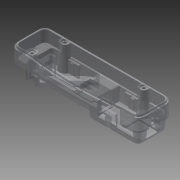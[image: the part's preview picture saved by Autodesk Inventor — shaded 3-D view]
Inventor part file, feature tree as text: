
AUTODESK INVENTOR PART (.ipt)
format: ipt  version: 2014 SP1 (Build 180222100, 222)  size: 1,254,400 bytes
history: native  units: mm
features: sketch x33, extrude x30, fillet x5, other x2, sweep x1, shell x1
ambient origin geometry x8: Origin, YZ Plane, XZ Plane, XY Plane, X Axis, Y Axis, Z Axis, Center Point
bodies: Solid1 (feature_tree)
feature tree (72):
  extrude  "MainShape"  Depth=38.0mm
  extrude  "LowerCurve"  Depth=70.0mm
  extrude  "RearShell"  Depth=8.0mm
  extrude  "LinkCableIndent"  Depth=3.5mm
  extrude  "LinkCableRecess"  Depth=30.0mm
  sweep  "LnkCableRecessSlanti"
  extrude  "ClipSlotsTop"  Depth=15.0mm
  extrude  "ClipSlotsBottom"  Depth=18.0mm
  extrude  "LinkCableSlot"  Depth=2.0mm
  shell  "HollowShell"  Thickness=2.0mm
  extrude  "USBCutout"  Depth=10.0mm
  extrude  "LinkCableCuttout"  Depth=13.5mm
  extrude  "LockingClipSlot"  Depth=16.0mm
  fillet  "RearRoundLarge"  Radius=9.0mm
  fillet  "RearRoundSmall"  Radius=3.0mm
  extrude  "PCBSideShelf"  TaperAngle=0.0deg  [1 undecoded]
  extrude  "PCBRearShelf"  TaperAngle=45.0deg  [1 undecoded]
  extrude  "PCBUSBShelf"  Depth=15.0mm
  extrude  "USBCutoutInternal"  TaperAngle=0.0deg  [1 undecoded]
  extrude  "FrontExtension"  TaperAngle=0.0deg  [1 undecoded]
  other  "FrontLip"
  extrude  "USBCuttoutReduction"  Depth=20.0mm
  extrude  "Extrusion19"  Depth=15.0mm
  fillet  "PCBInternalRadius"  Radius=33.0mm
  sketch  "Sketch22"  dims[d64=6.1mm d65=6.1mm]
  extrude  "RearLockingClip"  Depth=6.1mm
  extrude  "PCBSupport"  Depth=10.0mm
  extrude  "DCJackCuttout"  Depth=2.0mm
  extrude  "DCJackInternalSupport"  Depth=1.0mm
  extrude  "DCJackVoltageRef"  Depth=4.0mm TaperAngle=0.0deg
  extrude  "LabelIndent"  Depth=6.0mm
  other  "MountingBoss"
  extrude  "MountingBossLipCleanup"  Depth=2.0mm
  extrude  "MountingBossRearCleanup"  Depth=1.0mm
  fillet  "MountingBossRearRounds"  [1 undecoded]
  extrude  "LEDCutouts"  Depth=10.0mm
  extrude  "PCBEndstop"  Depth=10.0mm
  extrude  "PCBRearstop"  Depth=1.5mm
  extrude  "3DPrintingOptimisation"  Depth=15.0mm
  fillet  "3DPrinitingOptimisationRound"  Radius=12.0mm
  sketch  "Sketch2"  dims[d0=19.0mm d1=38.0mm]
  sketch  "Sketch4"  dims[d2=140.0mm d3=70.0mm]
  sketch  "Sketch5"  dims[d4=8.0mm d5=8.0mm]
  sketch  "Sketch6"  dims[d6=5.0mm d7=0.0mm d12=3.5mm]
  sketch  "Sketch7"  dims[d17=5.0mm d18=0.0mm d24=30.0mm]
  sketch  "Sketch8"  dims[d25=30.0mm d26=18.0mm]
  sketch  "Sketch9"  dims[d27=15.0mm d28=15.0mm]
  sketch  "Sketch10"  dims[d30=2.0mm d31=18.0mm]
  sketch  "Sketch11"  dims[d32=5.5mm d33=2.0mm d34=2.0mm]
  sketch  "Sketch12"  dims[d35=2.0mm d36=10.0mm]
  sketch  "Sketch13"  dims[d37=6.0mm d38=13.5mm d39=-0.872665mm]
  sketch  "Sketch14"  dims[d41=54.0mm d42=16.0mm d43=9.0mm d44=3.0mm]
  sketch  "Sketch15"  dims[d45=15.0mm d46=0.0mm d47=0.0mm]
  sketch  "Sketch16"  dims[d48=0.0mm d50=45.0deg]
  sketch  "Sketch17"  dims[d51=15.0mm d52=25.0mm]
  sketch  "Sketch18"  dims[d53=12.5mm d54=0.0mm d55=0.0mm]
  sketch  "Sketch19"  dims[d56=45.0deg d57=0.0mm]
  sketch  "Sketch20"  dims[d58=0.0mm d59=20.0mm]
  sketch  "Sketch21"  dims[d60=0.0mm d61=15.0mm d63=33.0mm]
  sketch  "Sketch23"  dims[d66=10.0mm d67=10.0mm]
  sketch  "Sketch24"  dims[d68=2.0mm d69=2.0mm]
  sketch  "Sketch25"  dims[d70=1.0mm d71=1.0mm]
  sketch  "Sketch26"  dims[d74=60.0mm d75=4.0mm d76=0.0mm]
  sketch  "Sketch27"  dims[d77=6.0mm d78=6.0mm]
  sketch  "Sketch28"  dims[d79=2.0mm d80=2.0mm]
  sketch  "Sketch29"  dims[d81=1.0mm d82=1.0mm d83=0.0mm]
  sketch  "Sketch32"  dims[d85=33.0mm d86=10.0mm]
  sketch  "Sketch33"  dims[d87=10.0mm d88=64.0mm]
  sketch  "Sketch34"  dims[d89=4.0mm d90=0.0mm d91=1.5mm]
  sketch  "Sketch35"  dims[d92=15.0mm d93=7.5mm d94=12.0mm]
  sketch  "Sketch36"  dims[d95=10.0mm d96=0.0mm]
  sketch  "Sketch37"  dims[d97=13.0mm d98=3.0mm d99=14.0mm d101=10.0mm d102=0.0mm d103=3.0mm d105=5.0mm d107=5.0mm d108=5.0mm d109=2.0mm d110=0.5mm d111=2.0mm d112=2.0mm d113=12.0mm d114=6.0mm d115=2.0mm d116=0.0mm d117=2.5mm d118=7.0mm d119=10.0mm d120=13.0mm d121=50.0mm d122=0.0mm d123=1.6mm d124=1.6mm d125=0.0mm d126=3.0mm d127=0.0mm d128=3.0mm d129=0.0mm d130=0.0mm d131=0.0mm d132=0.0mm d133=0.0mm d134=0.0mm d135=0.0mm d136=0.0mm d137=0.0mm d138=2.0mm d139=0.0mm d140=0.0mm d142=0.0mm d143=0.0mm d144=10.0mm d145=0.0mm d146=3.0mm d147=0.0mm d148=0.0mm d149=0.0mm d150=10.0mm d151=0.0mm d152=11.0mm d153=0.0mm d154=2.0mm d155=1.55mm d156=0.0mm d157=0.0mm d158=0.0mm d159=0.0mm d162=0.0mm d163=12.0mm d164=12.0mm d165=0.0mm d166=3.0mm d167=0.0mm d168=0.0mm d169=0.0mm d170=0.0mm d171=12.0mm d172=0.0mm d173=2.0mm d175=9.9mm d176=7.748994mm d177=2.0mm d178=5.748994mm d179=0.0mm d180=2.0mm d181=11.0mm d182=0.0mm d183=3.0mm d184=12.0mm d185=0.0mm d186=2.0mm d187=1.0mm d188=2.0mm d189=5.0mm d190=20.0mm d191=0.0mm d192=10.0mm d193=0.0mm d194=12.25mm d195=10.0mm d196=11.5mm d198=1.6mm d199=0.0mm d200=0.0mm d204=10.0mm d205=0.0mm d206=1.0mm d207=1.0mm d208=0.5mm d209=0.0mm d210=2.0mm d211=2.0mm d213=0.0mm d214=0.0mm d219=43.0mm d220=19.0mm d225=4.486241mm d226=4.486241mm d227=0.25mm d228=0.0mm d231=3.0mm d232=3.0mm d233=3.0mm d235=25.0mm d236=9.0mm d237=17.0mm d238=0.0mm d239=28.0mm d240=6.0mm d241=2.0mm d242=1.5mm d243=6.0mm d244=1.25mm d245=3.0mm d246=0.436332mm d247=0.436332mm d248=0.436332mm d249=0.436332mm d250=90.0deg d251=20.0mm d253=2.0mm d254=2.0mm d255=10.0mm d256=0.0mm d257=1.745329mm d258=0.436332mm d259=0.0mm d260=0.0mm d261=0.0mm d262=360.0deg d263=27.0mm d264=5.0mm d267=27.0mm d268=5.0mm d269=5.0mm d270=19.0mm d271=2.0mm d272=2.0mm d285=0.0mm d286=0.0mm d287=0.0mm d288=2.0mm d290=2.0mm d291=2.0mm d292=0.0mm d293=0.436332mm d294=1.0mm d295=3.0mm d296=3.0mm d297=4.0mm d298=4.0mm d299=2.5mm d300=4.5mm d301=10.0mm d302=0.0mm d303=2.0mm d304=2.0mm d305=0.0mm d306=102.0mm d307=4.0mm d308=4.0mm d309=2.0mm d310=10.0mm d311=0.0mm d312=0.0mm d313=0.0mm d314=0.0mm d315=2.0mm d316=10.0mm d317=0.0mm d318=5.0mm d319=0.0mm d321=0.0mm d322=0.0mm d323=10.0mm d324=0.0mm d325=0.0mm d326=2.0mm d327=2.0mm]
note: 5 required parameter values undecoded (feature->parameter linkage not recoverable at this tier; creation-order binding heuristic only, values carry confidence <= 0.55)
